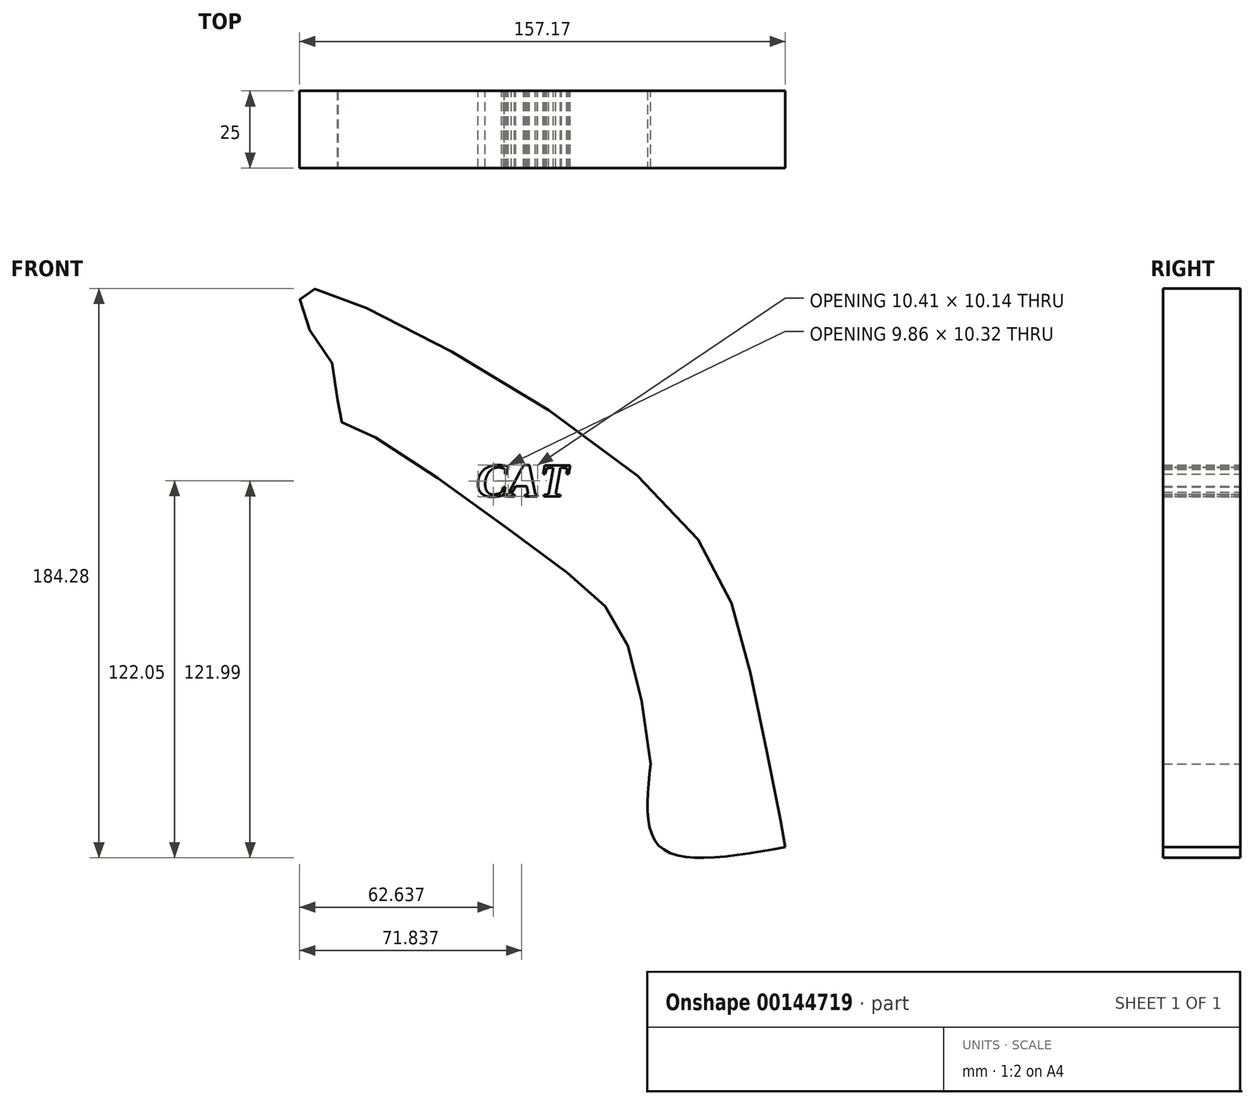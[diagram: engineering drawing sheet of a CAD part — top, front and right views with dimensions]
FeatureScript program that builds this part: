
annotation { "Feature Type Name" : "Feature", "Feature Type Description" : "" }
export const myFeature = defineFeature(function(context is Context, id is Id, definition is map)
    precondition{}
    {
        {
            var Q0;
            Q0=qCreatedBy(makeId("Front.planeOp"),FACE);
            var sketch = newSketch(context, id + "F0", { "sketchPlane" : qUnion([Q0])});
            skFitSpline(sketch, "E0", {"points": [v(28.7, -37.14) * mm, v(19.24, 6.08) * mm, v(-4.39, 29.37) * mm, v(-66.17, 71.57) * mm, v(-72.58, 74.95) * mm, v(-72.92, 88.79) * mm, v(-83, 105.67) * mm, v(-84.29, 115.45) * mm, v(-75.35, 115.45) * mm, v(31.83, 49.52) * mm, v(62.46, -14.28) * mm, v(72.24, -63.62) * mm, v(72.24, -64.04) * mm], "startDerivative": vector(-62.84, 480.75) * mm, "endDerivative": vector(-4.09, -23.51) * mm});
            skFitSpline(sketch, "E1", {"points": [v(72.24, -64.04) * mm, v(31.83, -63.97) * mm, v(28.7, -37.14) * mm], "startDerivative": vector(-91.73, -16.23) * mm, "endDerivative": vector(7.97, 73.03) * mm});
            skText(sketch, "E2", { "text": "CAT", "fontName": "Tinos-BoldItalic.ttf"});
            const initialGuessF0  = {"E2": [-0.02773, 0.04952, 1, 0, 0.01106]};
            skSetInitialGuess(sketch, initialGuessF0);
            skSolve(sketch);
        }
        {
            var Q0;
            Q0=makeQuery(id+"F0.imprint","IMPRINT",FACE,{"disambiguationData":[TD([[makeQuery(id+"F0.imprint","IMPRINT",EDGE,{"derivedFrom":sQuery(id+"F0.wireOp",EDGE,"E0")}),-1.0]])]});
            extrude(context, id + "F1", {"entities" : qUnion([Q0]), "depth" : 25 * mm});
        }
    });
